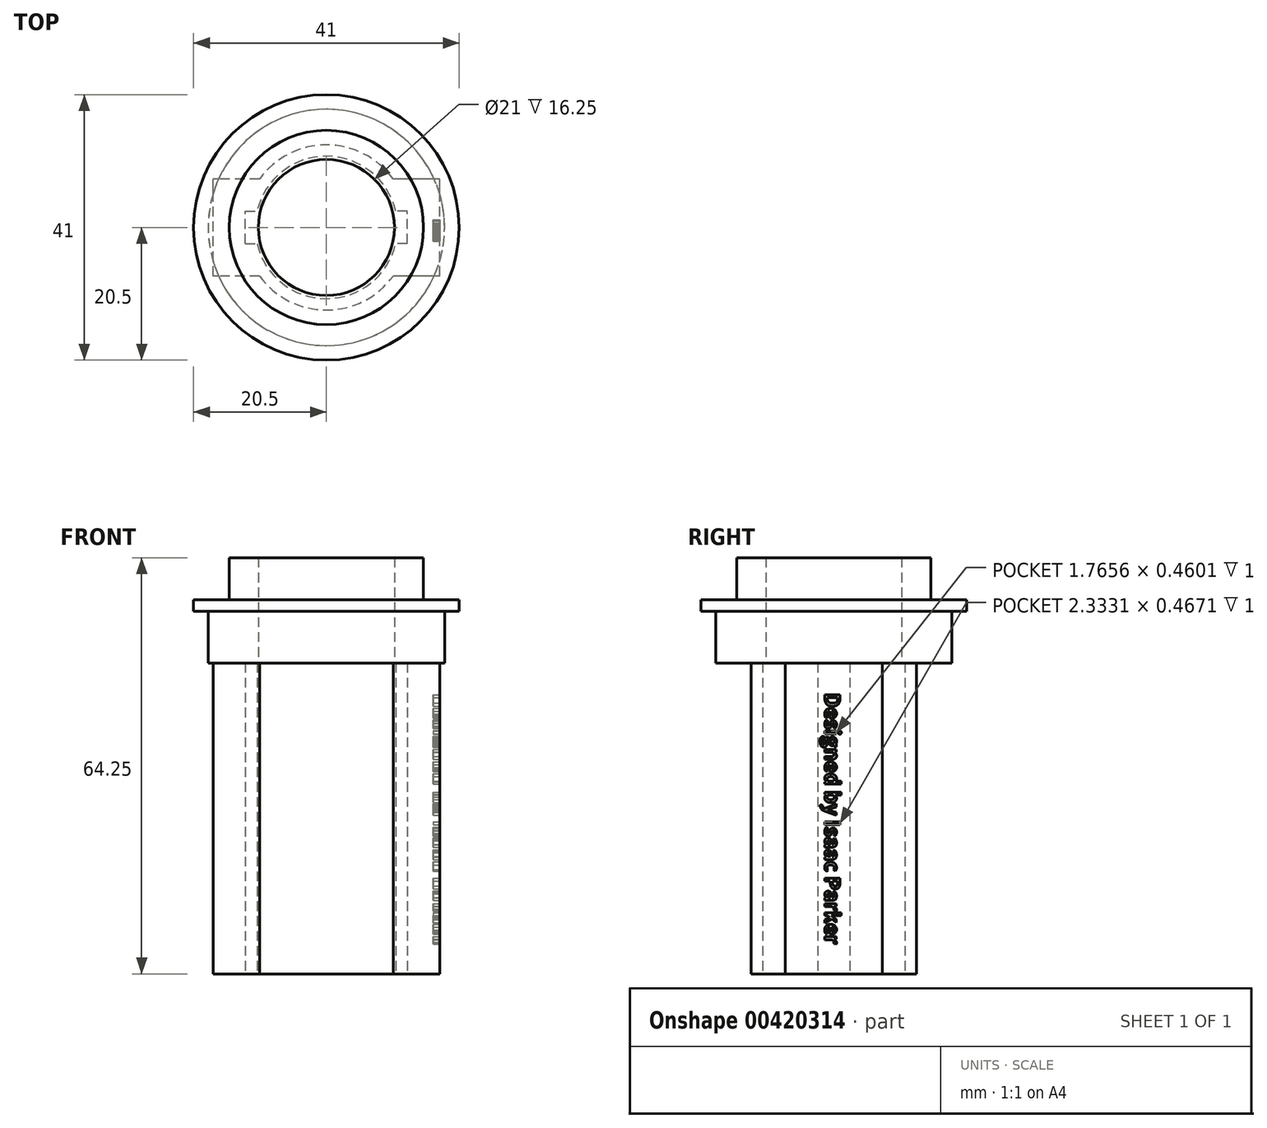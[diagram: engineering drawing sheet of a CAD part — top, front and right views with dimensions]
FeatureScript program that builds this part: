
annotation { "Feature Type Name" : "Feature", "Feature Type Description" : "" }
export const myFeature = defineFeature(function(context is Context, id is Id, definition is map)
    precondition{}
    {
        {
            var Q0;
            Q0=qCreatedBy(makeId("Top.planeOp"),FACE);
            var sketch = newSketch(context, id + "F0", { "sketchPlane" : qUnion([Q0])});
            skArc(sketch, "E0", {"start": v(-10.31, -7.5) * mm, "mid": v(0, -12.75) * mm, "end": v(10.31, -7.5) * mm});
            skArc(sketch, "E1", {"start": v(-10.71, -2.5) * mm, "mid": v(0, -11) * mm, "end": v(10.71, -2.5) * mm});
            skLineSegment(sketch, "E2.bottom", {"start": v(17.5, -7.5) * mm, "end": v(10.31, -7.5) * mm});
            skLineSegment(sketch, "E2.top", {"start": v(17.5, 7.5) * mm, "end": v(10.31, 7.5) * mm});
            skLineSegment(sketch, "E2.left", {"start": v(17.5, -7.5) * mm, "end": v(17.5, 7.5) * mm});
            skLineSegment(sketch, "E2.right", {"start": v(-17.5, -7.5) * mm, "end": v(-17.5, 7.5) * mm});
            skLineSegment(sketch, "E3.0", {"start": v(12.5, 2.5) * mm, "end": v(12.5, 2.5) * mm});
            skLineSegment(sketch, "E3.1", {"start": v(12.5, -2.5) * mm, "end": v(12.5, 2.5) * mm});
            skLineSegment(sketch, "E3.2", {"start": v(12.5, -2.5) * mm, "end": v(12.5, -2.5) * mm});
            skLineSegment(sketch, "E3.3", {"start": v(-12.5, -2.5) * mm, "end": v(-12.5, 2.5) * mm});
            skLineSegment(sketch, "E4.trimOffspring", {"start": v(-12.5, 2.5) * mm, "end": v(-12.5, 2.5) * mm});
            skLineSegment(sketch, "E5.trimOffspring", {"start": v(-12.5, -2.5) * mm, "end": v(-12.5, -2.5) * mm});
            skLineSegment(sketch, "E6", {"start": v(-12.5, 2.5) * mm, "end": v(-10.71, 2.5) * mm});
            skLineSegment(sketch, "E7", {"start": v(-12.5, -2.5) * mm, "end": v(-10.71, -2.5) * mm});
            skLineSegment(sketch, "E8", {"start": v(12.5, 2.5) * mm, "end": v(10.71, 2.5) * mm});
            skLineSegment(sketch, "E9", {"start": v(12.5, -2.5) * mm, "end": v(10.71, -2.5) * mm});
            skLineSegment(sketch, "E10.trimOffspring", {"start": v(-10.31, 7.5) * mm, "end": v(-17.5, 7.5) * mm});
            skArc(sketch, "E11.trimOffspring", {"start": v(10.31, 7.5) * mm, "mid": v(0, 12.75) * mm, "end": v(-10.31, 7.5) * mm});
            skArc(sketch, "E12.trimOffspring", {"start": v(10.71, 2.5) * mm, "mid": v(0, 11) * mm, "end": v(-10.71, 2.5) * mm});
            skLineSegment(sketch, "E13.trimOffspring", {"start": v(-10.31, -7.5) * mm, "end": v(-17.5, -7.5) * mm});
            skSolve(sketch);
        }
        {
            var Q0;
            Q0=makeQuery(id+"F0.imprint","IMPRINT",FACE,{"disambiguationData":[TD([[makeQuery(id+"F0.imprint","IMPRINT",EDGE,{"derivedFrom":sQuery(id+"F0.wireOp",EDGE,"E0")}),1.0]])]});
            extrude(context, id + "F1", {"entities" : qUnion([Q0]), "depth" : 48 * mm});
        }
        {
            var Q0;
            Q0=makeQuery(id+"F1.opExtrude","CAP_FACE",FACE,{"disambiguationData":[OSD([sQuery(id+"F0.wireOp",EDGE,"E0"),sQuery(id+"F0.wireOp",EDGE,"E1"),sQuery(id+"F0.wireOp",EDGE,"E2.bottom"),sQuery(id+"F0.wireOp",EDGE,"E2.top"),sQuery(id+"F0.wireOp",EDGE,"E2.left"),sQuery(id+"F0.wireOp",EDGE,"E2.right"),sQuery(id+"F0.wireOp",EDGE,"E3.0"),sQuery(id+"F0.wireOp",EDGE,"E3.1"),sQuery(id+"F0.wireOp",EDGE,"E3.2"),sQuery(id+"F0.wireOp",EDGE,"E3.3"),sQuery(id+"F0.wireOp",EDGE,"E4.trimOffspring"),sQuery(id+"F0.wireOp",EDGE,"E5.trimOffspring"),sQuery(id+"F0.wireOp",EDGE,"E6"),sQuery(id+"F0.wireOp",EDGE,"E7"),sQuery(id+"F0.wireOp",EDGE,"E8"),sQuery(id+"F0.wireOp",EDGE,"E9"),sQuery(id+"F0.wireOp",EDGE,"E10.trimOffspring"),sQuery(id+"F0.wireOp",EDGE,"E11.trimOffspring"),sQuery(id+"F0.wireOp",EDGE,"E12.trimOffspring"),sQuery(id+"F0.wireOp",EDGE,"E13.trimOffspring")])],"isStart":false});
            var sketch = newSketch(context, id + "F2", { "sketchPlane" : qUnion([Q0])});
            skCircle(sketch, "E14", {"center": v(0, 0) * mm, "radius": 18.25 * mm});
            skCircle(sketch, "E15", {"center": v(0, 0) * mm, "radius": 10.5 * mm});
            skSolve(sketch);
        }
        {
            var Q0;
            Q0=qSketchRegion(id+"F2",true);
            extrude(context, id + "F3", {"entities" : qUnion([Q0]), "operationType" : NewBodyOperationType.ADD, "depth" : 8 * mm});
        }
        {
            var Q0;
            Q0=makeQuery(id+"F3.opExtrude","CAP_FACE",FACE,{"disambiguationData":[OSD([sQuery(id+"F2.wireOp",EDGE,"E14"),sQuery(id+"F2.wireOp",EDGE,"E15")])],"isStart":false});
            var sketch = newSketch(context, id + "F4", { "sketchPlane" : qUnion([Q0])});
            skCircle(sketch, "E16", {"center": v(0, 0) * mm, "radius": 20.5 * mm});
            skCircle(sketch, "E17", {"center": v(0, 0) * mm, "radius": 10.5 * mm});
            skSolve(sketch);
        }
        {
            var Q0;
            Q0=qSketchRegion(id+"F4",true);
            var Q1;
            Q1=makeQuery(id+"F4.imprint","IMPRINT",FACE,{"disambiguationData":[TD([[makeQuery(id+"F4.imprint","IMPRINT",EDGE,{"derivedFrom":sQuery(id+"F4.wireOp",EDGE,"E17")}),-1.0]])]});
            extrude(context, id + "F5", {"entities" : qUnion([Q0, Q1]), "operationType" : NewBodyOperationType.ADD, "depth" : 1.75 * mm});
        }
        {
            var Q0;
            Q0=makeQuery(id+"F5.opExtrude","CAP_FACE",FACE,{"disambiguationData":[OSD([sQuery(id+"F4.wireOp",EDGE,"E16"),sQuery(id+"F4.wireOp",EDGE,"E17")])],"isStart":false});
            var sketch = newSketch(context, id + "F6", { "sketchPlane" : qUnion([Q0])});
            skCircle(sketch, "E18", {"center": v(0, 0) * mm, "radius": 15 * mm});
            skCircle(sketch, "E19", {"center": v(0, 0) * mm, "radius": 10.5 * mm});
            skSolve(sketch);
        }
        {
            var Q0;
            Q0=makeQuery(id+"F6.imprint","IMPRINT",FACE,{"disambiguationData":[TD([[makeQuery(id+"F6.imprint","IMPRINT",EDGE,{"derivedFrom":sQuery(id+"F6.wireOp",EDGE,"E18")}),1.0]])]});
            extrude(context, id + "F7", {"entities" : qUnion([Q0]), "operationType" : NewBodyOperationType.ADD, "depth" : 6.5 * mm});
        }
        {
            var Q0;
            Q0=makeQuery(id+"F1.opExtrude","SWEPT_FACE",FACE,{"disambiguationData":[OSD([sQuery(id+"F0.wireOp",EDGE,"E2.left")])]});
            var sketch = newSketch(context, id + "F8", { "sketchPlane" : qUnion([Q0])});
            skText(sketch, "E20", { "text": "Designed by Isaac Parker", "fontName": "NotoSansCJKsc-Bold.otf"});
            const initialGuessF8  = {"E20": [-0.00137, 0.0434, 0, -1, 0.00227]};
            skSetInitialGuess(sketch, initialGuessF8);
            skSolve(sketch);
        }
        {
            var Q0;
            Q0=qSketchRegion(id+"F8",true);
            extrude(context, id + "F9", {"entities" : qUnion([Q0]), "operationType" : NewBodyOperationType.REMOVE, "oppositeDirection" : true, "depth" : 1 * mm});
        }
    });
